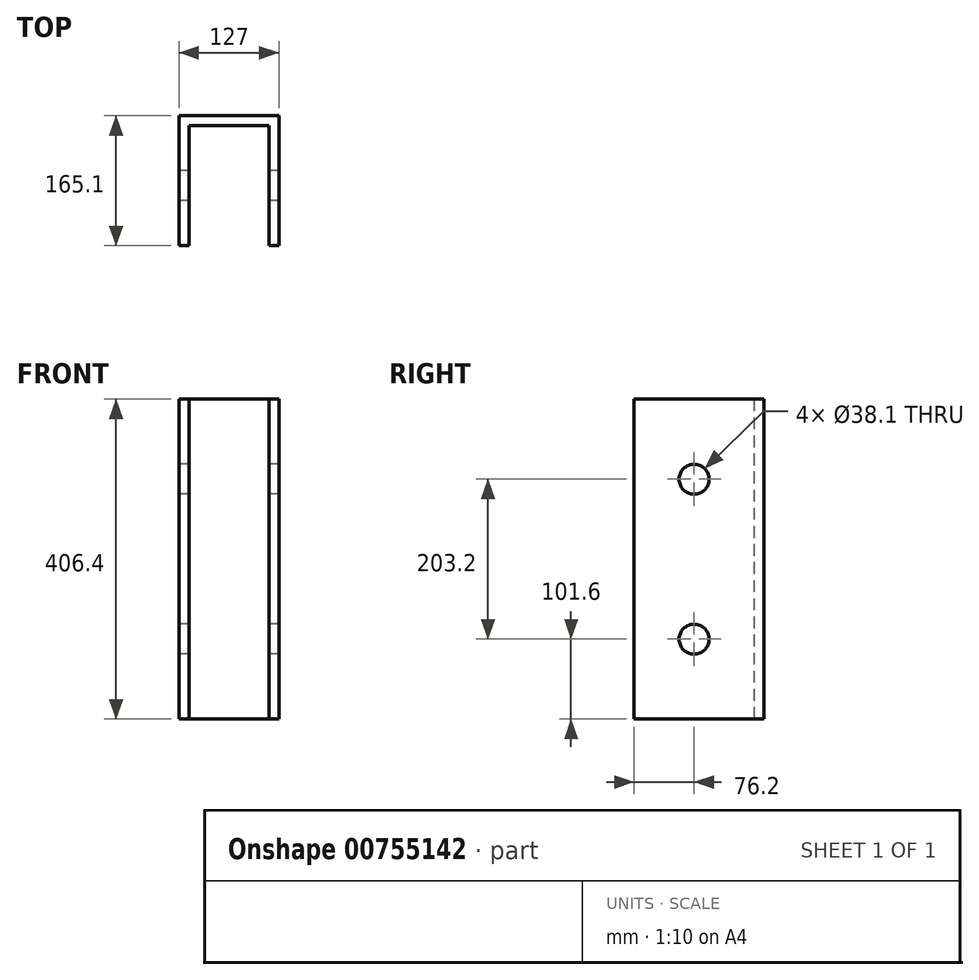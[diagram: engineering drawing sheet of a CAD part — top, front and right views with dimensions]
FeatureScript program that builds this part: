
annotation { "Feature Type Name" : "Feature", "Feature Type Description" : "" }
export const myFeature = defineFeature(function(context is Context, id is Id, definition is map)
    precondition{}
    {
        {
            var Q0;
            Q0=qCreatedBy(makeId("Right.planeOp"),FACE);
            var sketch = newSketch(context, id + "F0", { "sketchPlane" : qUnion([Q0])});
            skLineSegment(sketch, "E0.bottom", {"start": v(0, 0) * mm, "end": v(0, 0) * mm});
            skLineSegment(sketch, "E0.top", {"start": v(0, 0) * mm, "end": v(0, 0) * mm});
            skLineSegment(sketch, "E0.left", {"start": v(0, 0) * mm, "end": v(0, 0) * mm});
            skLineSegment(sketch, "E0.right", {"start": v(0, 0) * mm, "end": v(0, 0) * mm});
            skPoint(sketch, "E0.middle", {"position": v(0, 0) * mm});
            skLineSegment(sketch, "E1.bottom", {"start": v(76.2, 203.2) * mm, "end": v(-76.2, 203.2) * mm});
            skLineSegment(sketch, "E1.top", {"start": v(76.2, -203.2) * mm, "end": v(-76.2, -203.2) * mm});
            skLineSegment(sketch, "E1.left", {"start": v(76.2, 203.2) * mm, "end": v(76.2, -203.2) * mm});
            skLineSegment(sketch, "E1.right", {"start": v(-76.2, 203.2) * mm, "end": v(-76.2, -203.2) * mm});
            skCircle(sketch, "E2", {"center": v(0, 101.6) * mm, "radius": 19.05 * mm});
            skLineSegment(sketch, "E3.direction1", {"start": v(0, 101.6) * mm, "end": v(0, 101.6) * mm});
            skLineSegment(sketch, "E3.direction2", {"start": v(0, 82.55) * mm, "end": v(0, 101.6) * mm, "construction": true});
            skCircle(sketch, "E4", {"center": v(0, -101.6) * mm, "radius": 19.05 * mm});
            skLineSegment(sketch, "E5.trimOffspring", {"start": v(0, -101.6) * mm, "end": v(0, -82.55) * mm, "construction": true});
            skSolve(sketch);
        }
        {
            var Q0;
            Q0=makeQuery(id+"F0.imprint","IMPRINT",FACE,{"disambiguationData":[TD([[makeQuery(id+"F0.imprint","IMPRINT",EDGE,{"derivedFrom":sQuery(id+"F0.wireOp",EDGE,"E1.bottom")}),1.0]])]});
            extrude(context, id + "F1", {"entities" : qUnion([Q0]), "depth" : 12.7 * mm, "offsetDistance" : 25.4 * mm});
        }
        {
            var Q0;
            Q0=makeQuery(id+"F1.opExtrude","SWEPT_FACE",FACE,{"disambiguationData":[OSD([sQuery(id+"F0.wireOp",EDGE,"E1.left")])]});
            var sketch = newSketch(context, id + "F2", { "sketchPlane" : qUnion([Q0])});
            skLineSegment(sketch, "E6.bottom", {"start": v(0, 203.2) * mm, "end": v(-114.3, 203.2) * mm});
            skLineSegment(sketch, "E6.top", {"start": v(0, -203.2) * mm, "end": v(-114.3, -203.2) * mm});
            skLineSegment(sketch, "E6.left", {"start": v(0, 203.2) * mm, "end": v(0, -203.2) * mm});
            skLineSegment(sketch, "E6.right", {"start": v(-114.3, 203.2) * mm, "end": v(-114.3, -203.2) * mm});
            skSolve(sketch);
        }
        {
            var Q0;
            Q0 = qSketchRegion(id + "F2", true);
            extrude(context, id + "F3", {"entities" : qUnion([Q0]), "operationType" : NewBodyOperationType.ADD, "depth" : 12.7 * mm, "offsetDistance" : 25.4 * mm});
        }
        {
            var Q0;
            Q0=makeQuery(id+"F3.opExtrude","SWEPT_FACE",FACE,{"disambiguationData":[OSD([sQuery(id+"F2.wireOp",EDGE,"E6.right")])]});
            var sketch = newSketch(context, id + "F4", { "sketchPlane" : qUnion([Q0])});
            skSolve(sketch);
        }
        {
            var Q0;
            {var subQ0=sQuery(id+"F2.wireOp",EDGE,"E6.right");Q0=makeQuery(id+"F4.imprint","IMPRINT",FACE,{"disambiguationData":[TD([[makeQuery(id+"F4.imprint","IMPRINT",EDGE,{"derivedFrom":makeQuery(id+"F3.opExtrude","CAP_EDGE",EDGE,{"disambiguationData":[OSD([subQ0])],"isStart":true})}),1.0]])]});}
            var sketch = newSketch(context, id + "F5", { "sketchPlane" : qUnion([Q0])});
            skLineSegment(sketch, "E7.bottom", {"start": v(88.9, 203.2) * mm, "end": v(-76.2, 203.2) * mm});
            skLineSegment(sketch, "E7.top", {"start": v(88.9, -203.2) * mm, "end": v(-76.2, -203.2) * mm});
            skLineSegment(sketch, "E7.left", {"start": v(88.9, 203.2) * mm, "end": v(88.9, -203.2) * mm});
            skLineSegment(sketch, "E7.right", {"start": v(-76.2, 203.2) * mm, "end": v(-76.2, -203.2) * mm});
            skCircle(sketch, "E8.0", {"center": v(0, -101.6) * mm, "radius": 19.05 * mm});
            skCircle(sketch, "E8.1", {"center": v(0, 101.6) * mm, "radius": 19.05 * mm});
            skSolve(sketch);
        }
        {
            var Q0;
            Q0 = qSketchRegion(id + "F5", true);
            extrude(context, id + "F6", {"entities" : qUnion([Q0]), "operationType" : NewBodyOperationType.ADD, "depth" : 12.7 * mm, "offsetDistance" : 25.4 * mm});
        }
    });
